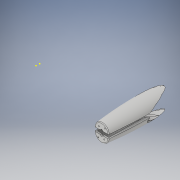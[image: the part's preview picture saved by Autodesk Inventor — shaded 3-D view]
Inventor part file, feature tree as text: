
AUTODESK INVENTOR PART (.ipt)
format: ipt  version: 2017 (Build 210142000, 142)  size: 2,275,840 bytes
history: native  units: in
note: dims shown in document units (in); Inventor stores cm internally (conversion verified against a paired STEP export)
features: reference x14, sketch x7, plane x6, other x6, extrude x4, projected_geometry x4, loft x1, fillet x1, surface_op x1, split x1, move_body x1
ambient origin geometry x8: Origin, YZ Plane, XZ Plane, XY Plane, X Axis, Y Axis, Z Axis, Center Point
bodies: Solid2 (feature_tree), Solid5 (feature_tree), Solid6 (feature_tree)
feature tree (46):
  plane  "Work Plane5"
  extrude  "Extrusion3"  Depth=1.4173in
  plane  "Work Plane7"
  loft  "Loft2"
  plane  "Work Plane8"
  extrude  "Extrusion4"  Depth=0.1181in
  extrude  "Extrusion8"  TaperAngle=90.0deg  [1 undecoded]
  plane  "Work Plane9"
  sketch  "Sketch15"  dims[d30=0.315in d31=0.0in d32=2.5in d33=3.8125in]
  sketch  "Sketch16"  dims[d34=0.0in d35=90.0deg]
  fillet  "Fillet1"  Radius=0.748in
  extrude  "Extrusion9"  Depth=2.5in
  surface_op  "Sculpt2"
  plane  "Work Plane10"
  split  "Split2"
  move_body  "Move Body2"
  sketch  "Sketch5"  dims[d21=2.7559in d22=1.4173in]
  reference  "Reference17"
  reference  "Reference18"
  reference  "Reference19"
  reference  "Reference20"
  reference  "Reference21"
  reference  "Reference22"
  reference  "Reference23"
  reference  "Reference24"
  reference  "Reference25"
  reference  "Reference26"
  reference  "Reference27"
  reference  "Reference28"
  reference  "Reference29"
  reference  "Reference30"
  plane  "Work Plane6"
  sketch  "Sketch6"  dims[d23=0.9843in d24=0.1181in]
  sketch  "Sketch7"  dims[d25=0.1181in d26=0.1181in]
  other  "Edges2"
  sketch  "Sketch14"  dims[d27=0.1181in d28=90.0deg d29=0.748in]
  projected_geometry  "Projected Loop4"
  projected_geometry  "Projected Loop5"
  projected_geometry  "Projected Loop6"
  sketch  "Sketch17"  dims[d36=0.0in d37=90.0deg d38=0.0in d39=90.0deg d40=0.9843in d41=0.748in d42=0.1181in d43=0.1181in d44=0.1181in d45=0.1181in d46=0.4975in d47=0.0in d62=-3.4375in d63=6.5438in d64=0.0in d67=0.0in d71=9.8425in d72=0.0787in d73=0.2362in d74=0.9188in d75=0.0in d76=0.25in d77=0.0in d78=0.3937in d79=0.0in]
  projected_geometry  "Projected Loop7"
  other  "<userpath>\Desktop\asa1\assembly.iam"
  other  "assembly.iam"
  other  "Part1:1"
  other  "Composite2"
  other  "Srf2"
note: 1 required parameter value undecoded (feature->parameter linkage not recoverable at this tier; creation-order binding heuristic only, values carry confidence <= 0.55)
